# Revit family: Epic Combi EPC110N-199N
name_source: partatom
category: Mechanical Equipment
revit_build: Autodesk Revit 2016 (Build: 20151007_0715(x64)
units: mm (PartAtom-declared; Revit-internal decimal feet)

## family parameters
Always vertical = Yes
Cut with Voids When Loaded = No
Part Type = Normal
Room Calculation Point = No
Round Connector Dimension = Use Diameter
Shared = No
Work Plane-Based = No

## types (3) — shared parameters
# of Electrical Connections = 1
AIR INLET = 3"
A_UNIT HEIGHT = 32 1/2"
BOILER WATER CONN = 1"
Bottom Clearance = 24"
C_UNIT DEPTH = 18"
Clearance Display = Yes
Condensate Diameter = 3/4"
DHW Diameter = 3/4"
Description = Epic Fire Tube Combi
E Vent Offset from Back = 2 3/4"
Electrical Offset from Back = 11 3/4"
Electrical Offset from Right = 3 1/2"
FUEL TYPE = NATURAL GAS
Front Clearance = 24"
Front Clearance Depth = 24"
Fuel Type = Natural or LP
GAS CONN = 1/2"
K Gas Offset from Back = 13 1/2"
Left Clearance = 12"
Manufacturer = Lochinvar
Right Clearance = 12"
SES BIM Studio # = 18 0649 05
Top Clearance = 6"
Total Amps = 2.2
URL = http://www.lochinvar.com
VENT SIZE = 3"
Voltage/Control = 24
Voltage/Heater = 120

## per-type parameters (varying)
| type | B_UNIT WIDTH | D Vent Offset from Right | G Combustion Air Offset from Back | GALLON CAPACITY | I Combustion Air Offset from Right | INPUT RATE (BTUH) | J Gas Offset from Left | L Condensate Offset from Back | M Water Offset from Back | N DHW Out Offset from Right | O Boiler Water In Offset from Right | OUTPUT RATE (BTUH) | P Condensate Offset from Right | Q Boiler Water Out Offset from Right | R Domestic In Offset from Right |
| EPC110N | 17 1/4" | 14 3/4" | 2 3/4" | 1.4 | 3 1/2" | 110,000 | 8 3/4" | 2 3/4" | 9" | 10 1/2" | 2 3/4" | 102,000 | 14 1/2" | 12 3/4" | 5" |
| EPC150N | 18 3/4" | 6 3/4" | 11 3/4" | 2.0 | 6 1/4" | 150,000 | 2 3/4" | 3" | 9" | 11 1/2" | 5" | 139,000 | 6 1/4" | 13 3/4" | 7 1/4" |
| EPC199N | 18 3/4" | 5 1/2" | 11 1/2" | 2.7 | 5 1/2" | 199,999 | 2 3/4" | 2 3/4" | 9 1/2" | 10 1/2" | 2 3/4" | 185,000 | 5 1/2" | 13" | 5 1/4" |

note: column(s) folded — value = type name in every type: MODEL NO., Model

## geometry (parser evidence)
native form markers: Sweep x2
no freeform markers — native parametric forms only
